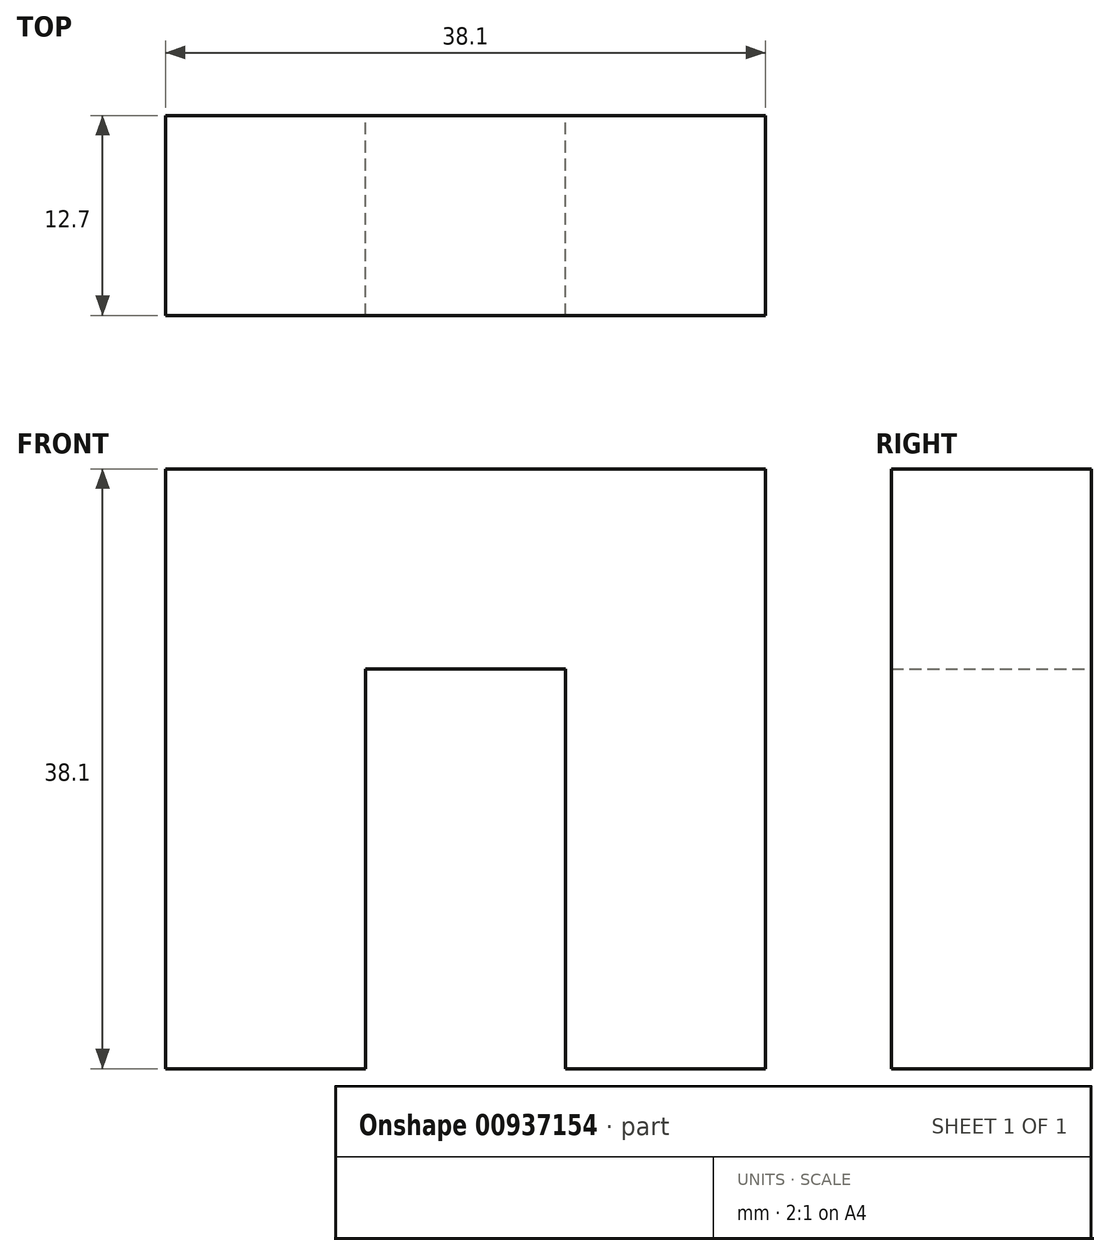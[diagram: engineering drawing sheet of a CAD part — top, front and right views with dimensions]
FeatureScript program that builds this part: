
annotation { "Feature Type Name" : "Feature", "Feature Type Description" : "" }
export const myFeature = defineFeature(function(context is Context, id is Id, definition is map)
    precondition{}
    {
        {
            var Q0;
            Q0=qCreatedBy(makeId("Front.planeOp"),FACE);
            var sketch = newSketch(context, id + "F0", { "sketchPlane" : qUnion([Q0])});
            skLineSegment(sketch, "E0.bottom", {"start": v(-19.05, 17.24) * mm, "end": v(-6.35, 17.24) * mm});
            skLineSegment(sketch, "E0.top", {"start": v(-19.05, 4.54) * mm, "end": v(-6.35, 4.54) * mm});
            skLineSegment(sketch, "E0.left", {"start": v(-19.05, 17.24) * mm, "end": v(-19.05, 4.54) * mm});
            skLineSegment(sketch, "E0.right", {"start": v(-6.35, 17.24) * mm, "end": v(-6.35, 4.54) * mm});
            skLineSegment(sketch, "E1.top", {"start": v(-19.05, -8.16) * mm, "end": v(-6.35, -8.16) * mm});
            skLineSegment(sketch, "E1.left", {"start": v(-19.05, 4.54) * mm, "end": v(-19.05, -8.16) * mm});
            skLineSegment(sketch, "E1.right", {"start": v(-6.35, 4.54) * mm, "end": v(-6.35, -8.16) * mm});
            skLineSegment(sketch, "E2.top", {"start": v(-19.05, -20.86) * mm, "end": v(-6.35, -20.86) * mm});
            skLineSegment(sketch, "E2.left", {"start": v(-19.05, -8.16) * mm, "end": v(-19.05, -20.86) * mm});
            skLineSegment(sketch, "E2.right", {"start": v(-6.35, -8.16) * mm, "end": v(-6.35, -20.86) * mm});
            skLineSegment(sketch, "E3.bottom", {"start": v(-6.35, 17.24) * mm, "end": v(6.35, 17.24) * mm});
            skLineSegment(sketch, "E3.top", {"start": v(-6.35, 4.54) * mm, "end": v(6.35, 4.54) * mm});
            skLineSegment(sketch, "E3.right", {"start": v(6.35, 17.24) * mm, "end": v(6.35, 4.54) * mm});
            skLineSegment(sketch, "E4.bottom", {"start": v(6.35, 17.24) * mm, "end": v(19.05, 17.24) * mm});
            skLineSegment(sketch, "E4.top", {"start": v(6.35, 4.54) * mm, "end": v(19.05, 4.54) * mm});
            skLineSegment(sketch, "E4.right", {"start": v(19.05, 17.24) * mm, "end": v(19.05, 4.54) * mm});
            skLineSegment(sketch, "E5.top", {"start": v(6.35, -8.16) * mm, "end": v(19.05, -8.16) * mm});
            skLineSegment(sketch, "E5.left", {"start": v(6.35, 4.54) * mm, "end": v(6.35, -8.16) * mm});
            skLineSegment(sketch, "E5.right", {"start": v(19.05, 4.54) * mm, "end": v(19.05, -8.16) * mm});
            skLineSegment(sketch, "E6.bottom", {"start": v(19.05, -8.16) * mm, "end": v(6.35, -8.16) * mm});
            skLineSegment(sketch, "E6.top", {"start": v(19.05, -20.86) * mm, "end": v(6.35, -20.86) * mm});
            skLineSegment(sketch, "E6.left", {"start": v(19.05, -8.16) * mm, "end": v(19.05, -20.86) * mm});
            skLineSegment(sketch, "E6.right", {"start": v(6.35, -8.16) * mm, "end": v(6.35, -20.86) * mm});
            skSolve(sketch);
        }
        {
            var Q0;
            Q0 = qSketchRegion(id + "F0", true);
            extrude(context, id + "F1", {"entities" : qUnion([Q0]), "endBound" : BoundingType.SYMMETRIC, "depth" : 12.7 * mm, "offsetDistance" : 25.4 * mm});
        }
    });
